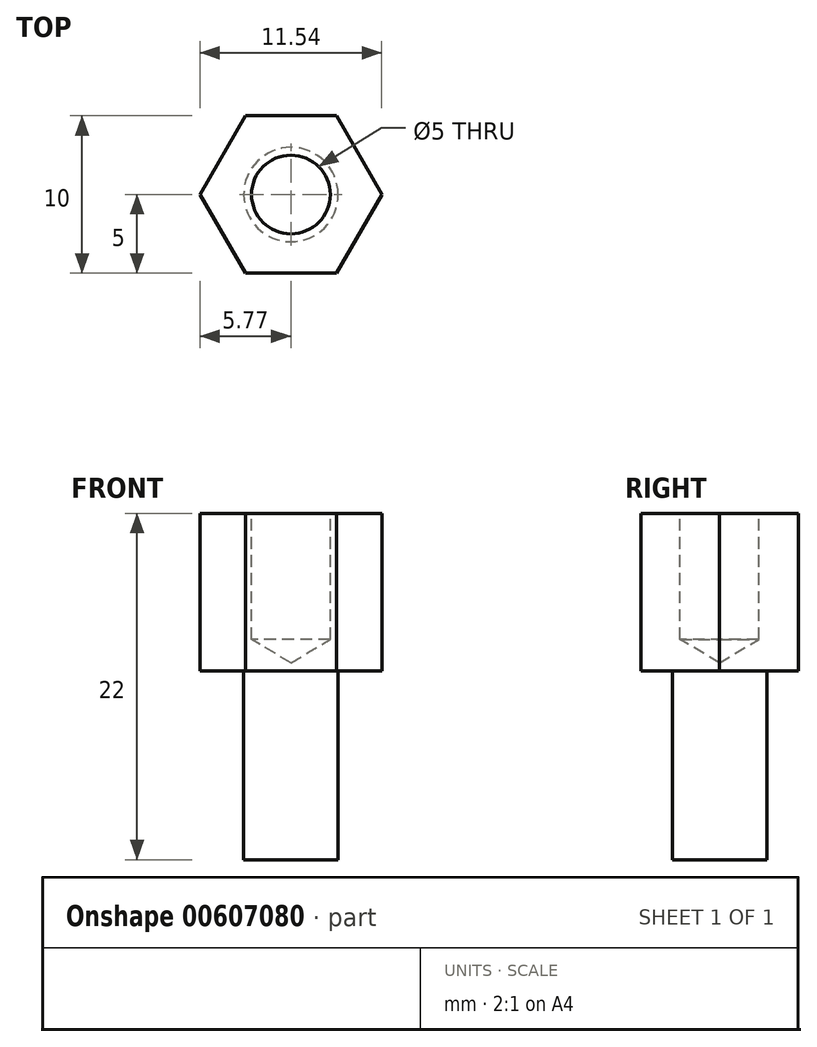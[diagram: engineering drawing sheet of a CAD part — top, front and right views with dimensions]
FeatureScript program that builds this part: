
annotation { "Feature Type Name" : "Feature", "Feature Type Description" : "" }
export const myFeature = defineFeature(function(context is Context, id is Id, definition is map)
    precondition{}
    {
        {
            var Q0;
            Q0=qCreatedBy(makeId("Top.planeOp"),FACE);
            var sketch = newSketch(context, id + "F0", { "sketchPlane" : qUnion([Q0]) });
            skCircle(sketch, "E0.cCircle", {"center": v(0, 0) * mm, "radius": 5 * mm, "construction": true});
            skLineSegment(sketch, "E0.0", {"start": v(-2.89, 5) * mm, "end": v(2.89, 5) * mm});
            skLineSegment(sketch, "E0.1", {"start": v(2.89, 5) * mm, "end": v(5.77, 0) * mm});
            skLineSegment(sketch, "E0.2", {"start": v(5.77, 0) * mm, "end": v(2.89, -5) * mm});
            skLineSegment(sketch, "E0.3", {"start": v(2.89, -5) * mm, "end": v(-2.89, -5) * mm});
            skLineSegment(sketch, "E0.4", {"start": v(-2.89, -5) * mm, "end": v(-5.77, 0) * mm});
            skLineSegment(sketch, "E0.5", {"start": v(-5.77, 0) * mm, "end": v(-2.89, 5) * mm});
            skPoint(sketch, "E0.0.midPoint", {"position": v(0, 5) * mm});
            skSolve(sketch);
        }
        {
            var Q0;
            Q0=makeQuery(id+"F0.imprint","IMPRINT",FACE,{"disambiguationData":[TD([[makeQuery(id+"F0.imprint","IMPRINT",EDGE,{"derivedFrom":sQuery(id+"F0.wireOp",EDGE,"E0.0")}),-1.0]])]});
            extrude(context, id + "F1", {"entities" : qUnion([Q0]), "depth" : 10 * mm, "offsetDistance" : 25 * mm});
        }
        {
            var Q0;
            Q0=makeQuery(id+"F1.opExtrude","CAP_FACE",FACE,{"disambiguationData":[OSD([sQuery(id+"F0.wireOp",EDGE,"E0.0"),sQuery(id+"F0.wireOp",EDGE,"E0.1"),sQuery(id+"F0.wireOp",EDGE,"E0.2"),sQuery(id+"F0.wireOp",EDGE,"E0.3"),sQuery(id+"F0.wireOp",EDGE,"E0.4"),sQuery(id+"F0.wireOp",EDGE,"E0.5")])],"isStart":false});
            var sketch = newSketch(context, id + "F2", { "sketchPlane" : qUnion([Q0]) });
            skPoint(sketch, "E1", {"position": v(0, 0) * mm});
            skSolve(sketch);
        }
        {
            var Q0;
            Q0=sQuery(id+"F2.wireOp",VERTEX,"E1");
            var Q1;
            Q1=makeQuery(id+"F1.opExtrude","SWEPT_BODY",BODY,{"disambiguationData":[OSD([sQuery(id+"F0.wireOp",EDGE,"E0.0"),sQuery(id+"F0.wireOp",EDGE,"E0.1"),sQuery(id+"F0.wireOp",EDGE,"E0.2"),sQuery(id+"F0.wireOp",EDGE,"E0.3"),sQuery(id+"F0.wireOp",EDGE,"E0.4"),sQuery(id+"F0.wireOp",EDGE,"E0.5")])]});
            hole(context, id + "F3", {"style" : HoleStyle.SIMPLE, "endStyle" : HoleEndStyle.BLIND, "standardTappedOrClearance" : lookupTablePath({ "standard" : "ISO", "engagement" : "75%", "pitch" : "1 mm", "size" : "M6", "type" : "Tapped" }), "standardBlindInLast" : lookupTablePath({ "standard" : "ISO", "fit" : "Normal", "engagement" : "75%", "pitch" : "1 mm", "size" : "M6", "type" : "Clearance & tapped" }), "holeDiameter" : 5 * mm, "majorDiameter" : 6 * mm, "showTappedDepth" : true, "holeDepth" : 8 * mm, "isTappedThrough" : true, "tappedDepth" : 8 * mm, "tapClearance" : 0, "startFromSketch" : true, "locations" : qUnion([Q0]), "scope" : qUnion([Q1])});
        }
        {
            var Q0;
            Q0=makeQuery(id+"F1.opExtrude","CAP_FACE",FACE,{"disambiguationData":[OSD([sQuery(id+"F0.wireOp",EDGE,"E0.0"),sQuery(id+"F0.wireOp",EDGE,"E0.1"),sQuery(id+"F0.wireOp",EDGE,"E0.2"),sQuery(id+"F0.wireOp",EDGE,"E0.3"),sQuery(id+"F0.wireOp",EDGE,"E0.4"),sQuery(id+"F0.wireOp",EDGE,"E0.5")])],"isStart":true});
            var sketch = newSketch(context, id + "F4", { "sketchPlane" : qUnion([Q0]) });
            skCircle(sketch, "E2", {"center": v(0, 0) * mm, "radius": 3 * mm});
            skSolve(sketch);
        }
        {
            var Q0;
            Q0 = qSketchRegion(id + "F4", true);
            extrude(context, id + "F5", {"entities" : qUnion([Q0]), "operationType" : NewBodyOperationType.ADD, "depth" : 12 * mm, "offsetDistance" : 25 * mm});
        }
    });
